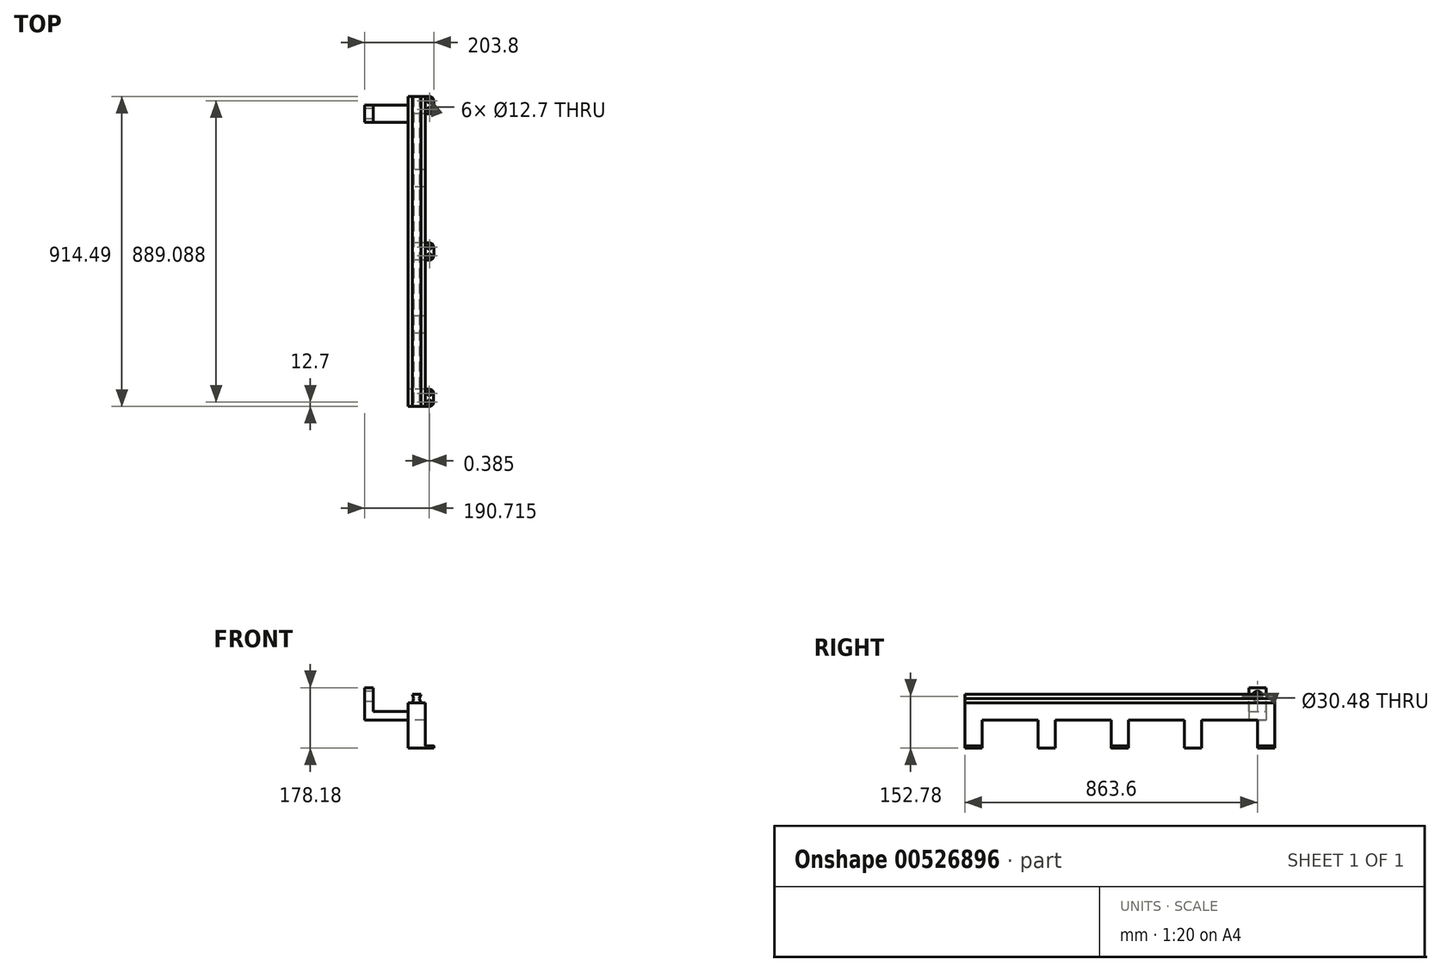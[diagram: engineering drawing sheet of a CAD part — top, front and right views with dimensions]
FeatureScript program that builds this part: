
annotation { "Feature Type Name" : "Feature", "Feature Type Description" : "" }
export const myFeature = defineFeature(function(context is Context, id is Id, definition is map)
    precondition{}
    {
        {
            var Q0;
            Q0=qCreatedBy(makeId("Right.planeOp"),FACE);
            var sketch = newSketch(context, id + "F0", { "sketchPlane" : qUnion([Q0])});
            skLineSegment(sketch, "E0", {"start": v(0, 0) * mm, "end": v(914.4, 0) * mm});
            skLineSegment(sketch, "E1", {"start": v(914.4, -133.73) * mm, "end": v(863.6, -133.73) * mm});
            skLineSegment(sketch, "E2", {"start": v(863.6, -50.8) * mm, "end": v(698.5, -50.8) * mm});
            skLineSegment(sketch, "E3", {"start": v(698.5, -50.8) * mm, "end": v(698.5, -133.73) * mm});
            skLineSegment(sketch, "E4", {"start": v(698.5, -133.73) * mm, "end": v(647.7, -133.73) * mm});
            skLineSegment(sketch, "E5", {"start": v(647.7, -133.73) * mm, "end": v(647.7, -50.8) * mm});
            skLineSegment(sketch, "E6", {"start": v(647.7, -50.8) * mm, "end": v(482.6, -50.8) * mm});
            skLineSegment(sketch, "E7", {"start": v(482.6, -50.8) * mm, "end": v(482.6, -133.73) * mm});
            skPoint(sketch, "E7.endSnap0", {"position": v(673.1, -133.73) * mm});
            skLineSegment(sketch, "E8", {"start": v(482.6, -133.73) * mm, "end": v(431.8, -133.73) * mm});
            skLineSegment(sketch, "E9", {"start": v(431.8, -133.73) * mm, "end": v(431.8, -50.8) * mm});
            skLineSegment(sketch, "E10", {"start": v(431.8, -50.8) * mm, "end": v(266.7, -50.8) * mm});
            skLineSegment(sketch, "E11", {"start": v(266.7, -50.8) * mm, "end": v(266.7, -133.73) * mm});
            skLineSegment(sketch, "E12", {"start": v(266.7, -133.73) * mm, "end": v(215.9, -133.73) * mm});
            skLineSegment(sketch, "E13", {"start": v(215.9, -133.73) * mm, "end": v(215.9, -50.8) * mm});
            skLineSegment(sketch, "E14", {"start": v(215.9, -50.8) * mm, "end": v(50.8, -50.8) * mm});
            skLineSegment(sketch, "E15", {"start": v(50.8, -50.8) * mm, "end": v(50.8, -133.73) * mm});
            skLineSegment(sketch, "E16", {"start": v(50.8, -133.73) * mm, "end": v(0, -133.73) * mm});
            skLineSegment(sketch, "E17", {"start": v(914.4, 0) * mm, "end": v(914.4, -133.73) * mm});
            skLineSegment(sketch, "E18", {"start": v(0, 0) * mm, "end": v(0, -133.73) * mm});
            skLineSegment(sketch, "E19", {"start": v(863.6, -50.8) * mm, "end": v(863.6, -133.73) * mm});
            skSolve(sketch);
        }
        {
            var Q0;
            Q0=makeQuery(id+"F0.imprint","IMPRINT",FACE,{"disambiguationData":[TD([[makeQuery(id+"F0.imprint","IMPRINT",EDGE,{"derivedFrom":sQuery(id+"F0.wireOp",EDGE,"E0")}),-1.0]])]});
            extrude(context, id + "F1", {"entities" : qUnion([Q0]), "depth" : 50.8 * mm, "offsetDistance" : 25.4 * mm});
        }
        {
            var Q0;
            Q0=qCreatedBy(makeId("Front.planeOp"),FACE);
            var sketch = newSketch(context, id + "F2", { "sketchPlane" : qUnion([Q0])});
            skLineSegment(sketch, "E20", {"start": v(0, 0) * mm, "end": v(12.7, 0) * mm});
            skLineSegment(sketch, "E21.bottom", {"start": v(12.7, 0) * mm, "end": v(38.1, 0) * mm});
            skLineSegment(sketch, "E22", {"start": v(12.7, 25.4) * mm, "end": v(38.1, 25.4) * mm});
            skLineSegment(sketch, "E23", {"start": v(12.7, 0) * mm, "end": v(16.63, 12.7) * mm});
            skLineSegment(sketch, "E24", {"start": v(16.63, 12.7) * mm, "end": v(12.7, 25.4) * mm});
            skLineSegment(sketch, "E25", {"start": v(25.4, 25.4) * mm, "end": v(25.4, 0) * mm, "construction": true});
            skLineSegment(sketch, "E26.MirrorCS", {"start": v(34.17, 12.7) * mm, "end": v(38.1, 25.4) * mm});
            skLineSegment(sketch, "E27.MirrorCS", {"start": v(38.1, 0) * mm, "end": v(34.17, 12.7) * mm});
            skSolve(sketch);
        }
        {
            var Q0;
            Q0=makeQuery(id+"F2.imprint","IMPRINT",FACE,{"disambiguationData":[TD([[makeQuery(id+"F2.imprint","IMPRINT",EDGE,{"derivedFrom":sQuery(id+"F2.wireOp",EDGE,"E21.bottom")}),1.0]])]});
            extrude(context, id + "F3", {"entities" : qUnion([Q0]), "oppositeDirection" : true, "depth" : 914.4 * mm, "offsetDistance" : 25.4 * mm});
        }
        {
            var Q0;
            Q0=qCreatedBy(makeId("Front.planeOp"),FACE);
            cPlane(context, id + "F4", {"entities" : qUnion([Q0]), "cplaneType" : CPlaneType.OFFSET, "offset" : 838.2 * mm, "oppositeDirection" : true, "width" : 152.4 * mm, "height" : 152.4 * mm});
        }
        {
            var Q0;
            Q0=qCreatedBy(id+"F4.planeOp",FACE);
            var sketch = newSketch(context, id + "F5", { "sketchPlane" : qUnion([Q0])});
            skLineSegment(sketch, "E28", {"start": v(0, 0) * mm, "end": v(0, -50.8) * mm});
            skLineSegment(sketch, "E29", {"start": v(-102.11, -25.4) * mm, "end": v(50.29, -25.4) * mm});
            skLineSegment(sketch, "E30", {"start": v(-127.51, -50.8) * mm, "end": v(50.29, -50.8) * mm});
            skLineSegment(sketch, "E31", {"start": v(-102.11, -25.4) * mm, "end": v(-102.11, 44.45) * mm});
            skLineSegment(sketch, "E32", {"start": v(-102.11, 44.45) * mm, "end": v(-127.51, 44.45) * mm});
            skLineSegment(sketch, "E33", {"start": v(50.29, -50.8) * mm, "end": v(50.29, -25.4) * mm});
            skLineSegment(sketch, "E34", {"start": v(-127.51, 44.45) * mm, "end": v(-127.51, -50.8) * mm});
            skSolve(sketch);
        }
        {
            var Q0;
            Q0 = qSketchRegion(id + "F5", true);
            extrude(context, id + "F6", {"entities" : qUnion([Q0]), "operationType" : NewBodyOperationType.ADD, "oppositeDirection" : true, "depth" : 50.8 * mm, "offsetDistance" : 25.4 * mm});
        }
        {
            var Q0;
            Q0=makeQuery(id+"F1.opExtrude","SWEPT_FACE",FACE,{"disambiguationData":[OSD([sQuery(id+"F0.wireOp",EDGE,"E16")])]});
            cPlane(context, id + "F7", {"entities" : qUnion([Q0]), "cplaneType" : CPlaneType.OFFSET, "offset" : 0 * mm, "width" : 152.4 * mm, "height" : 152.4 * mm});
        }
        {
            var Q0;
            Q0=qCreatedBy(id+"F7.planeOp",FACE);
            var sketch = newSketch(context, id + "F8", { "sketchPlane" : qUnion([Q0])});
            skLineSegment(sketch, "E35", {"start": v(50.5, 0) * mm, "end": v(50.5, -50.8) * mm});
            skLineSegment(sketch, "E36", {"start": v(50.5, -50.8) * mm, "end": v(63.2, -50.8) * mm});
            skLineSegment(sketch, "E37", {"start": v(75.9, -38.1) * mm, "end": v(75.9, -12.7) * mm});
            skLineSegment(sketch, "E38", {"start": v(63.2, 0) * mm, "end": v(50.5, 0) * mm});
            skPoint(sketch, "E39.visualSharp", {"position": v(75.9, 0) * mm});
            skArc(sketch, "E39.filletArc", {"start": v(75.9, -12.7) * mm, "mid": v(72.19, -3.72) * mm, "end": v(63.2, 0) * mm});
            skPoint(sketch, "E40.visualSharp", {"position": v(75.9, -50.8) * mm});
            skArc(sketch, "E40.filletArc", {"start": v(63.2, -50.8) * mm, "mid": v(72.19, -47.08) * mm, "end": v(75.9, -38.1) * mm});
            skCircle(sketch, "E41", {"center": v(63.2, -12.7) * mm, "radius": 6.35 * mm});
            skCircle(sketch, "E42", {"center": v(63.2, -38.1) * mm, "radius": 6.35 * mm});
            skLineSegment(sketch, "E43", {"start": v(50.72, -431.77) * mm, "end": v(50.72, -482.57) * mm});
            skLineSegment(sketch, "E44", {"start": v(50.72, -482.57) * mm, "end": v(63.42, -482.57) * mm});
            skLineSegment(sketch, "E45", {"start": v(76.12, -469.87) * mm, "end": v(76.12, -444.47) * mm});
            skLineSegment(sketch, "E46", {"start": v(63.42, -431.77) * mm, "end": v(50.72, -431.77) * mm});
            skPoint(sketch, "E47.visualSharp", {"position": v(76.12, -431.77) * mm});
            skArc(sketch, "E47.filletArc", {"start": v(76.12, -444.47) * mm, "mid": v(72.4, -435.5) * mm, "end": v(63.42, -431.77) * mm});
            skPoint(sketch, "E48.visualSharp", {"position": v(76.12, -482.57) * mm});
            skArc(sketch, "E48.filletArc", {"start": v(63.42, -482.57) * mm, "mid": v(72.4, -478.85) * mm, "end": v(76.12, -469.87) * mm});
            skCircle(sketch, "E49", {"center": v(63.42, -444.47) * mm, "radius": 6.35 * mm});
            skCircle(sketch, "E50", {"center": v(63.42, -469.87) * mm, "radius": 6.35 * mm});
            skLineSegment(sketch, "E51", {"start": v(50.9, -914.49) * mm, "end": v(50.9, -863.69) * mm});
            skLineSegment(sketch, "E52", {"start": v(50.9, -863.69) * mm, "end": v(63.6, -863.69) * mm});
            skLineSegment(sketch, "E53", {"start": v(76.3, -876.39) * mm, "end": v(76.3, -901.79) * mm});
            skLineSegment(sketch, "E54", {"start": v(63.6, -914.49) * mm, "end": v(50.9, -914.49) * mm});
            skPoint(sketch, "E55.visualSharp", {"position": v(76.3, -863.69) * mm});
            skArc(sketch, "E55.filletArc", {"start": v(76.3, -876.39) * mm, "mid": v(72.57, -867.4) * mm, "end": v(63.6, -863.69) * mm});
            skPoint(sketch, "E56.visualSharp", {"position": v(76.3, -914.49) * mm});
            skArc(sketch, "E56.filletArc", {"start": v(63.6, -914.49) * mm, "mid": v(72.57, -910.77) * mm, "end": v(76.3, -901.79) * mm});
            skCircle(sketch, "E57", {"center": v(63.6, -876.39) * mm, "radius": 6.35 * mm});
            skCircle(sketch, "E58", {"center": v(63.6, -901.79) * mm, "radius": 6.35 * mm});
            skSolve(sketch);
        }
        {
            var Q0;
            Q0 = qSketchRegion(id + "F8", true);
            extrude(context, id + "F9", {"entities" : qUnion([Q0]), "operationType" : NewBodyOperationType.ADD, "oppositeDirection" : true, "depth" : 6.35 * mm, "offsetDistance" : 25.4 * mm});
        }
        {
            var Q0;
            Q0 = qBodyType(qCreatedBy(id + "F3J1oGdN4Sv03Rn_5" ,EDGE), BodyType.WIRE);
            var Q1;
            Q1=makeQuery(id+"F6.opExtrude","SWEPT_FACE",FACE,{"disambiguationData":[OSD([sQuery(id+"F5.wireOp",EDGE,"E34")])]});
            cPlane(context, id + "F10", {"entities" : qUnion([Q0, Q1]), "cplaneType" : CPlaneType.OFFSET, "offset" : 0 * mm, "width" : 152.4 * mm, "height" : 152.4 * mm});
        }
        {
            var Q0;
            Q0=qCreatedBy(id+"F10.planeOp",FACE);
            var sketch = newSketch(context, id + "F11", { "sketchPlane" : qUnion([Q0])});
            skCircle(sketch, "E59", {"center": v(-863.6, 19.05) * mm, "radius": 15.24 * mm});
            skSolve(sketch);
        }
        {
            var Q0;
            Q0 = qSketchRegion(id + "F11", true);
            extrude(context, id + "F12", {"entities" : qUnion([Q0]), "operationType" : NewBodyOperationType.REMOVE, "oppositeDirection" : true, "depth" : 25.4 * mm, "offsetDistance" : 25.4 * mm});
        }
    });
